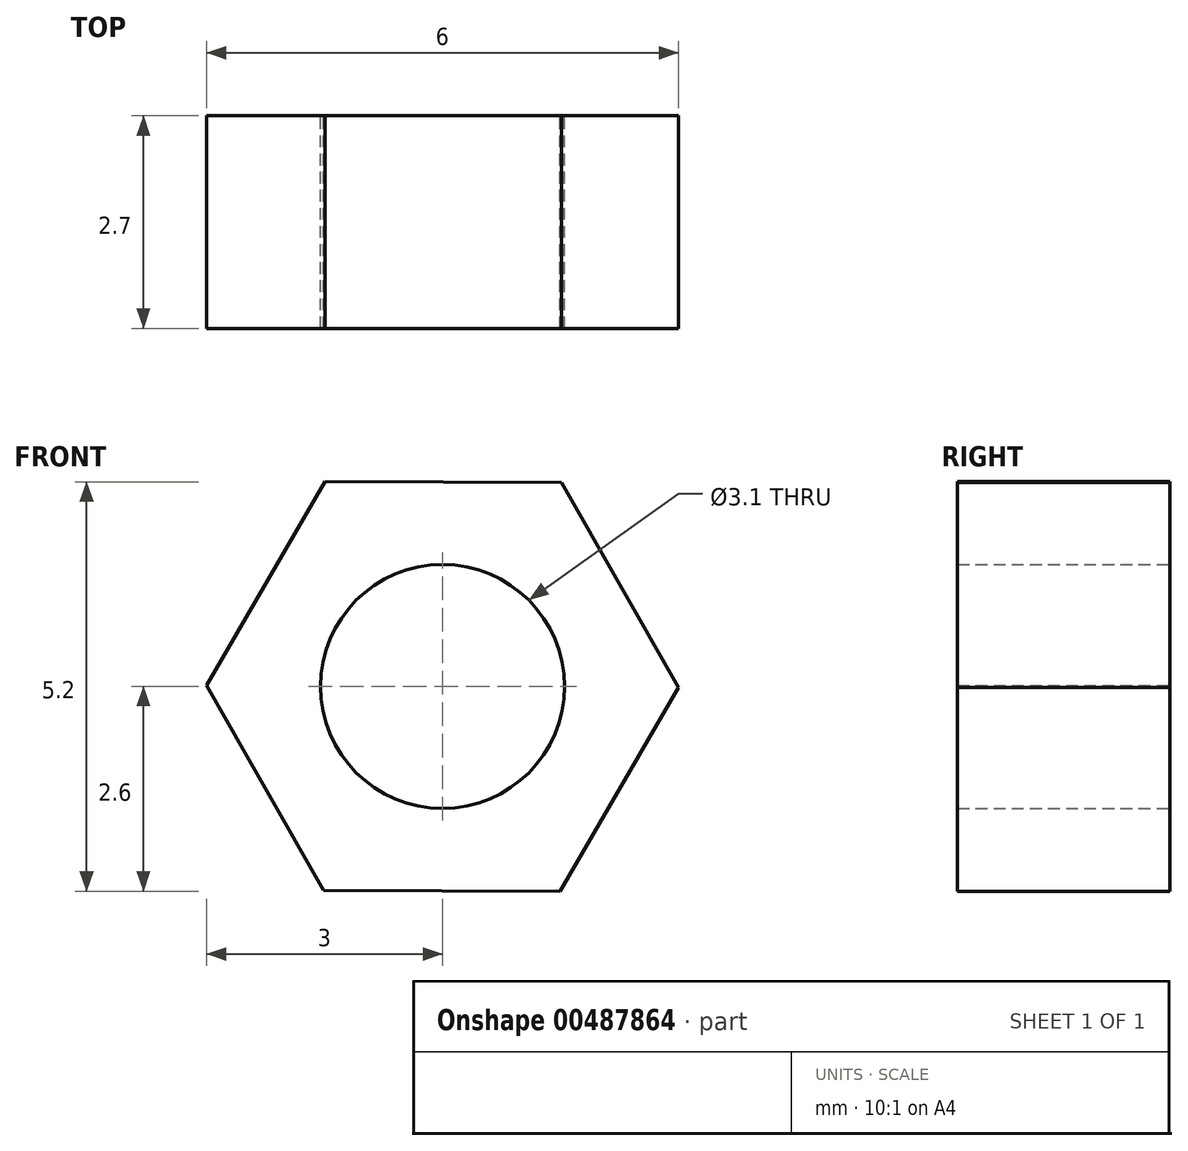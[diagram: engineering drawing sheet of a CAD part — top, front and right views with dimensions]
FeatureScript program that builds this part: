
annotation { "Feature Type Name" : "Feature", "Feature Type Description" : "" }
export const myFeature = defineFeature(function(context is Context, id is Id, definition is map)
    precondition{}
    {
        {
            var Q0;
            Q0=qCreatedBy(makeId("Front.planeOp"),FACE);
            var sketch = newSketch(context, id + "F0", { "sketchPlane" : qUnion([Q0])});
            skCircle(sketch, "E0.cCircle", {"center": v(0, 0) * mm, "radius": 2.6 * mm, "construction": true});
            skLineSegment(sketch, "E0.0", {"start": v(1.51, 2.6) * mm, "end": v(3, -0.01) * mm});
            skLineSegment(sketch, "E0.1", {"start": v(3, -0.01) * mm, "end": v(1.49, -2.6) * mm});
            skLineSegment(sketch, "E0.2", {"start": v(1.49, -2.6) * mm, "end": v(-1.51, -2.6) * mm});
            skLineSegment(sketch, "E0.3", {"start": v(-1.51, -2.6) * mm, "end": v(-3, 0.01) * mm});
            skLineSegment(sketch, "E0.4", {"start": v(-3, 0.01) * mm, "end": v(-1.49, 2.6) * mm});
            skLineSegment(sketch, "E0.5", {"start": v(-1.49, 2.6) * mm, "end": v(1.51, 2.6) * mm});
            skPoint(sketch, "E0.0.midPoint", {"position": v(2.26, 1.3) * mm});
            skCircle(sketch, "E1", {"center": v(0, 0) * mm, "radius": 1.55 * mm});
            skSolve(sketch);
        }
        {
            var Q0;
            Q0 = qSketchRegion(id + "F0", true);
            extrude(context, id + "F1", {"entities" : qUnion([Q0]), "depth" : 2.7 * mm});
        }
    });
